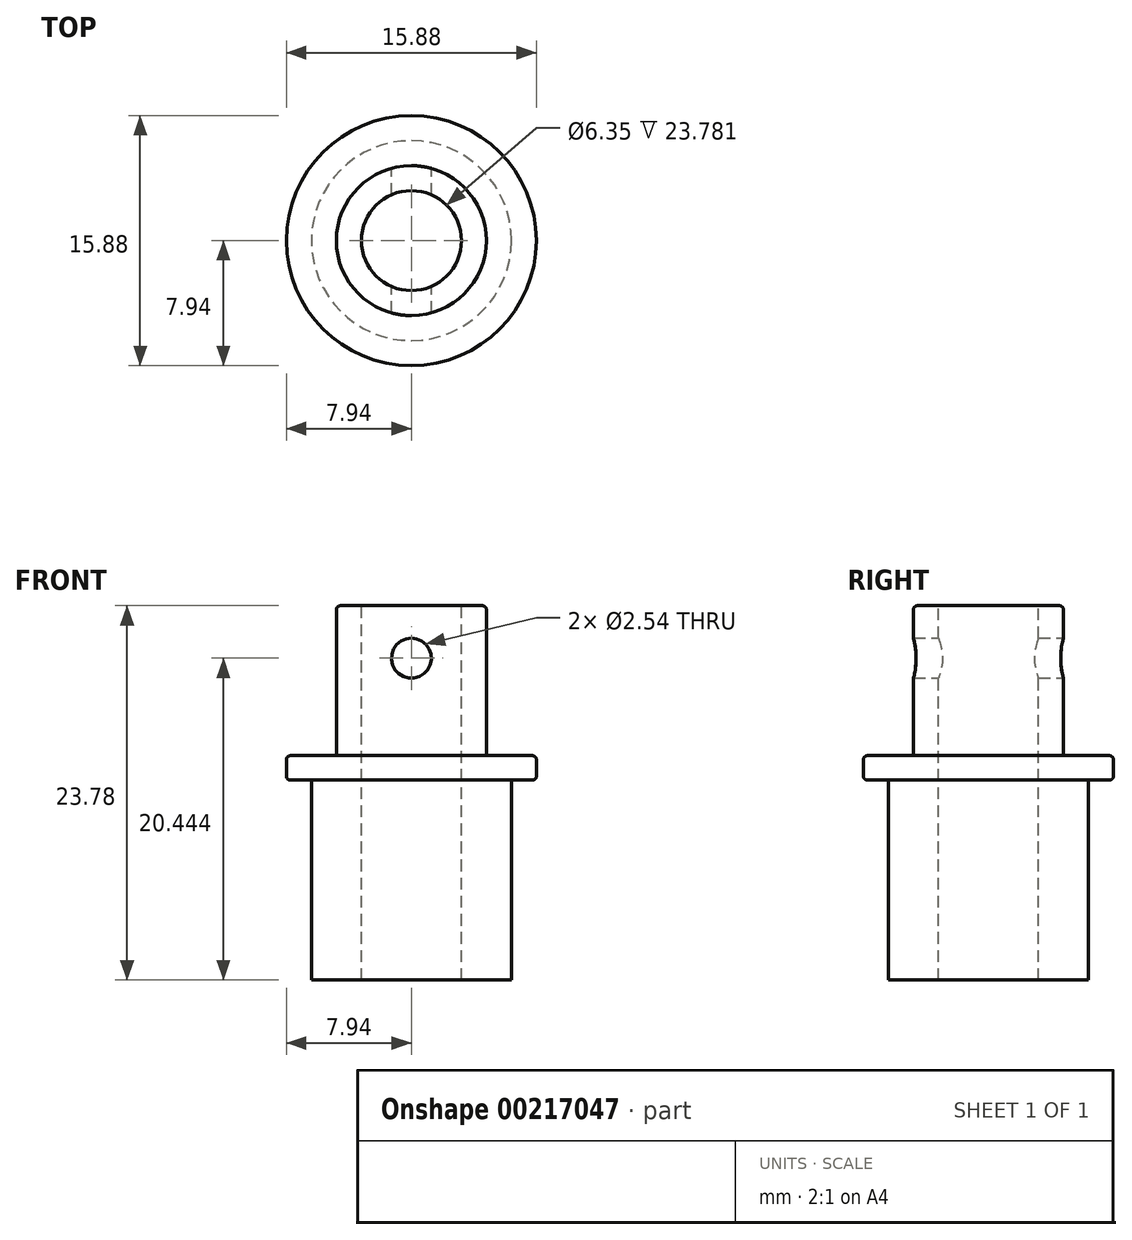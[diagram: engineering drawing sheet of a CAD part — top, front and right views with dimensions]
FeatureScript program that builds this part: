
annotation { "Feature Type Name" : "Feature", "Feature Type Description" : "" }
export const myFeature = defineFeature(function(context is Context, id is Id, definition is map)
    precondition{}
    {
        {
            var Q0;
            Q0=qCreatedBy(makeId("Top.planeOp"),FACE);
            var sketch = newSketch(context, id + "F0", { "sketchPlane" : qUnion([Q0])});
            skCircle(sketch, "E0", {"center": v(0, 0) * mm, "radius": 6.35 * mm});
            skSolve(sketch);
        }
        {
            var Q0;
            Q0 = qSketchRegion(id + "F0", true);
            extrude(context, id + "F1", {"entities" : qUnion([Q0]), "oppositeDirection" : true, "depth" : 12.7 * mm});
        }
        {
            var Q0;
            Q0=makeQuery(id+"F1.opExtrude","CAP_FACE",FACE,{"disambiguationData":[OSD([sQuery(id+"F0.wireOp",EDGE,"E0")])],"isStart":true});
            var sketch = newSketch(context, id + "F2", { "sketchPlane" : qUnion([Q0])});
            skCircle(sketch, "E1", {"center": v(0, 0) * mm, "radius": 7.94 * mm});
            skSolve(sketch);
        }
        {
            var Q0;
            Q0 = qSketchRegion(id + "F2", true);
            extrude(context, id + "F3", {"entities" : qUnion([Q0]), "operationType" : NewBodyOperationType.ADD, "depth" : 1.56 * mm});
        }
        {
            var Q0;
            Q0=makeQuery(id+"F3.opExtrude","CAP_FACE",FACE,{"disambiguationData":[OSD([sQuery(id+"F2.wireOp",EDGE,"E1")])],"isStart":false});
            var sketch = newSketch(context, id + "F4", { "sketchPlane" : qUnion([Q0])});
            skCircle(sketch, "E2", {"center": v(0, 0) * mm, "radius": 4.76 * mm});
            skSolve(sketch);
        }
        {
            var Q0;
            Q0=makeQuery(id+"F4.imprint","IMPRINT",FACE,{"disambiguationData":[TD([[makeQuery(id+"F4.imprint","IMPRINT",EDGE,{"derivedFrom":sQuery(id+"F4.wireOp",EDGE,"E2")}),1.0]])]});
            extrude(context, id + "F5", {"entities" : qUnion([Q0]), "operationType" : NewBodyOperationType.ADD, "depth" : 9.52 * mm});
        }
        {
            var Q0;
            Q0=makeQuery(id+"F3.opExtrude","CAP_EDGE",EDGE,{"disambiguationData":[OSD([sQuery(id+"F2.wireOp",EDGE,"E1")])],"isStart":false});
            var Q1;
            Q1=makeQuery(id+"F3.opExtrude","CAP_EDGE",EDGE,{"disambiguationData":[OSD([sQuery(id+"F2.wireOp",EDGE,"E1")])],"isStart":true});
            var Q2;
            Q2=makeQuery(id+"F5.opExtrude","CAP_EDGE",EDGE,{"disambiguationData":[OSD([sQuery(id+"F4.wireOp",EDGE,"E2")])],"isStart":false});
            fillet(context, id + "F6", {"entities" : qUnion([Q0, Q1, Q2]), "radius" : 0.25 * mm, "tangentPropagation" : true, "allowEdgeOverflow" : false});
        }
        {
            var Q0;
            Q0=qCreatedBy(makeId("Front.planeOp"),FACE);
            var sketch = newSketch(context, id + "F7", { "sketchPlane" : qUnion([Q0])});
            skCircle(sketch, "E3", {"center": v(0, 7.74) * mm, "radius": 1.27 * mm});
            skSolve(sketch);
        }
        {
            var Q0;
            Q0 = qSketchRegion(id + "F7", true);
            extrude(context, id + "F8", {"entities" : qUnion([Q0]), "operationType" : NewBodyOperationType.REMOVE, "depth" : 25.4 * mm, "symmetric" : true});
        }
        {
            var Q0;
            Q0=makeQuery(id+"F5.opExtrude","CAP_FACE",FACE,{"disambiguationData":[OSD([sQuery(id+"F4.wireOp",EDGE,"E2")])],"isStart":false});
            var sketch = newSketch(context, id + "F9", { "sketchPlane" : qUnion([Q0])});
            skCircle(sketch, "E4", {"center": v(0, 0) * mm, "radius": 3.18 * mm});
            skSolve(sketch);
        }
        {
            var Q0;
            Q0=makeQuery(id+"F9.imprint","IMPRINT",FACE,{"disambiguationData":[TD([[makeQuery(id+"F9.imprint","IMPRINT",EDGE,{"derivedFrom":sQuery(id+"F9.wireOp",EDGE,"E4")}),1.0]])]});
            extrude(context, id + "F10", {"entities" : qUnion([Q0]), "operationType" : NewBodyOperationType.REMOVE, "endBound" : BoundingType.THROUGH_ALL, "oppositeDirection" : true, "depth" : 25.4 * mm});
        }
    });
